# Revit family: F-08BTWT_v1.0 20241031 1720
name_source: partatom
category: Communication Devices
units: mm (PartAtom-declared; Revit-internal decimal feet)

## family parameters
Always vertical = Yes
Cut with Voids When Loaded = No
Maintain Annotation Orientation = No
Part Type = Normal
Room Calculation Point = No
Round Connector Dimension = Use Diameter
Shared = No
Work Plane-Based = No

## types (2) — shared parameters
Accessory = Speaker bracket ···1, Base bracket ···1, Base bracket cover ···1, Bracket fixing screw ···1 set
Crossover Frequency = 3kHz
Depth = 164 mm  [stored 0.538058 ft]
Dimensions = 251 (W) X 392 (H) X 216 (D) mm (9.88" X 15.43" X 8.5")
Directivty Angle = Horizontal: 100°, Vertical: 100°
Enclosure = Bass-reflex type
Frequency Response = 50 Hz - 20 kHz, -10 dB at installation in 1 /2 free sound field
Height = 274 mm  [stored 0.89895 ft]
Input Termina = Push-in terminal
Instollation Environment = Indoor installation
Manufacturer = TOA
Operoting Temperature = -10 °C to +50 °C (14 °F to 122 °F)
Option - Speaker Stand = ST-34B Note: K&M 19780 or K&M 19610 is required.
Power Handling Capacity = Rated noise power: 90 W (8 Ω), Continuous program: 180 W (8 Ω)
Product info = https://www.toa-products.com
Rated Impedance (100V line) = 170 Ω (60 W), 330 Ω (30 W), 670 Ω (15 W), 3.3 kΩ (3 W)
Rated Impedance (70V line) = 83 Ω (60 W), 170 Ω (30 W), 330 Ω (15 W), 670 Ω (7.5 W), 3.3 kΩ (1.5 W)
Rated Impedance (Low) = 8 Ω
Rated Input = 60 W (100 V line, 70 V line)
Sensitivty = 91 dB (1 W, 1 m) at installation in 1/2 free sound field
Speaker Component (high frequency) = 25 mm (1") dome tweeter
Speaker Component (low frequency) = 20 cm ( 8") PPcone-type
URL = https://www.toa.jp
Update Info = https://www.sound-toa.com
Weight = 5.2 kg (11.46 lb)
Width = 162 mm  [stored 0.531496 ft]
バージョン = 1.0
zero-valued in all types: Default Elevation

## per-type parameters (varying)
| type | Body | Finish - Base bracket | Finish - Base bracket cover | Finish - Enclosure | Finish - Grille | Finish - Speaker bracket | Grille | Model | Option - Adapter plate |
| F-08BT (Black) | TOA-Body(Black) | Steel plate, t4, black (RAL 9011 equivalent), paint | HIPS, black (RAL 9011 equivalent) | HIPS, black (RAL 9011 equivalent), paint | Aluminum, black (RAL 9011 equivalent), pain | Die-cast aluminum, black (RAL 9011 equivalent), paint | TOA-Grille(Black) | F-08BT | HY-F08B |
| F-08WT (White) | TOA-Body(White) | Steel plate, t4, white (RAL 9016 equivalent), paint | HIPS, white (RAL 9016 equivalent | HIPS, white (RAL 9016 equivalent), paint | Aluminum, white (RAL 9016 equivalent), paint | Die-cast aluminum, white (RAL 9016 equivalent), paint | TOA-Grille(White) | F-08WT | HY-F08W |

note: [stored X ft] marks values corroborated as IEEE doubles in the binary element streams (Revit-internal decimal feet)
